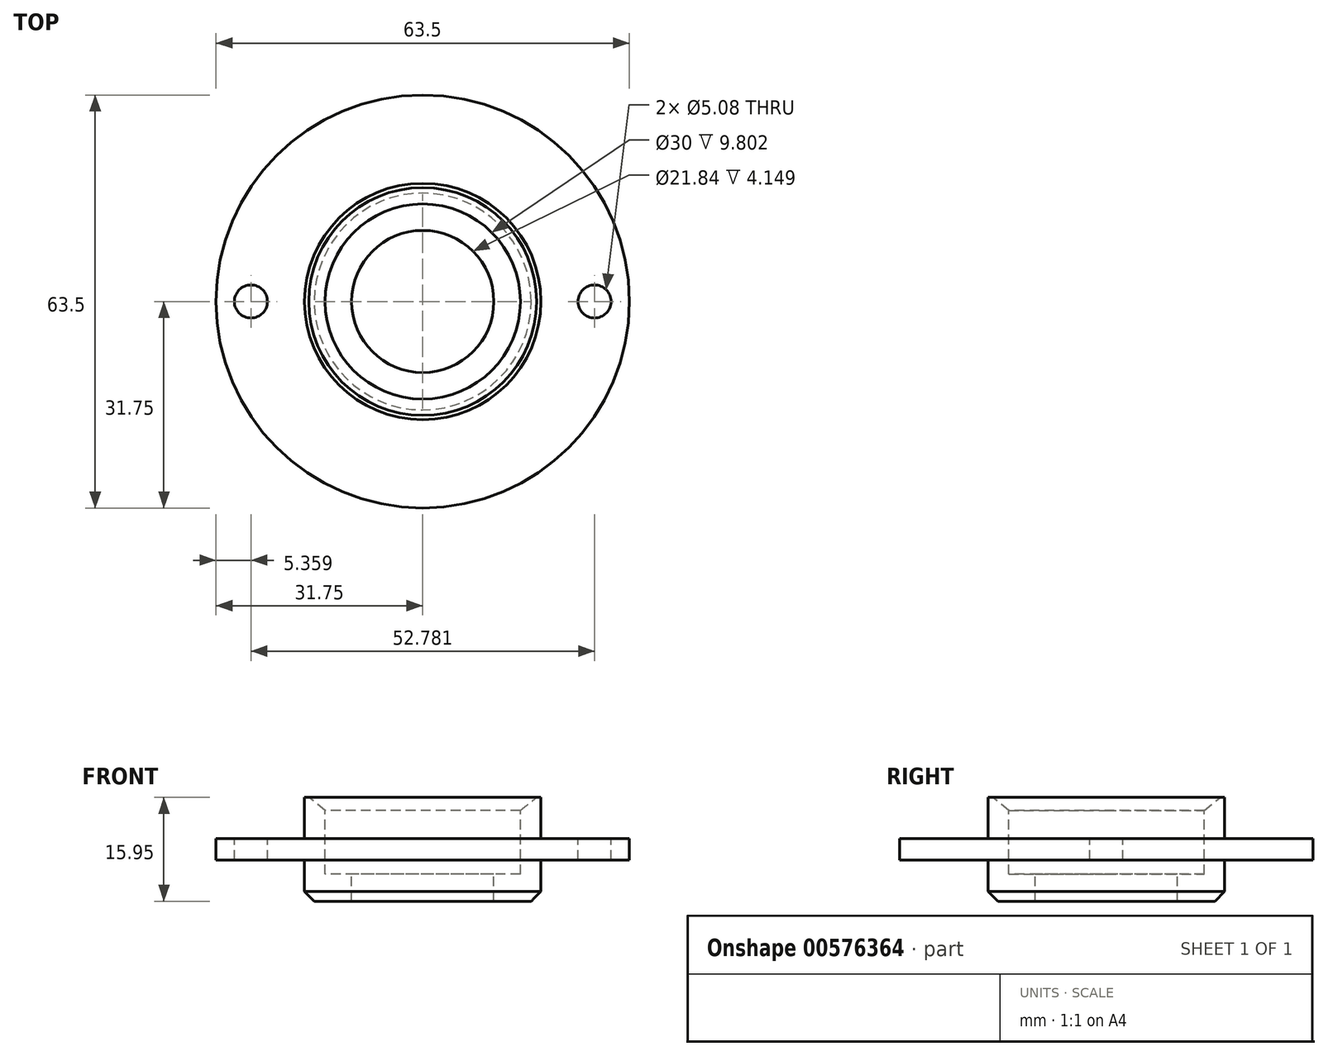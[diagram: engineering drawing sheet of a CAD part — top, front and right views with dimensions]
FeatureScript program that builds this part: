
annotation { "Feature Type Name" : "Feature", "Feature Type Description" : "" }
export const myFeature = defineFeature(function(context is Context, id is Id, definition is map)
    precondition{}
    {
        {
            var Q0;
            Q0=qCreatedBy(makeId("Front.planeOp"),FACE);
            var sketch = newSketch(context, id + "F0", { "sketchPlane" : qUnion([Q0])});
            skLineSegment(sketch, "E0", {"start": v(0, 6.57) * mm, "end": v(0, -16.88) * mm, "construction": true});
            skLineSegment(sketch, "E1", {"start": v(31.75, -2.73) * mm, "end": v(31.75, -5.98) * mm});
            skLineSegment(sketch, "E2", {"start": v(18.16, 3.62) * mm, "end": v(18.16, -2.73) * mm});
            skLineSegment(sketch, "E3", {"start": v(18.16, -5.98) * mm, "end": v(18.16, -12.33) * mm});
            skLineSegment(sketch, "E4", {"start": v(18.16, -2.73) * mm, "end": v(31.75, -2.73) * mm});
            skLineSegment(sketch, "E5", {"start": v(18.16, -5.98) * mm, "end": v(31.75, -5.98) * mm});
            skLineSegment(sketch, "E6", {"start": v(10.92, -12.33) * mm, "end": v(10.92, -8.18) * mm});
            skLineSegment(sketch, "E7", {"start": v(15, -8.18) * mm, "end": v(10.92, -8.18) * mm});
            skLineSegment(sketch, "E8", {"start": v(15, -8.18) * mm, "end": v(15, 3.62) * mm});
            skLineSegment(sketch, "E9", {"start": v(15, 3.62) * mm, "end": v(18.16, 3.62) * mm});
            skLineSegment(sketch, "E10", {"start": v(10.92, -12.33) * mm, "end": v(18.16, -12.33) * mm});
            skSolve(sketch);
        }
        {
            var Q0;
            Q0 = qSketchRegion(id + "F0", true);
            var Q1;
            Q1=sQuery(id+"F0.wireOp",EDGE,"E0");
            revolve(context, id + "F1", {"surfaceOperationType" : NewSurfaceOperationType.NEW, "entities" : qUnion([Q0]), "axis" : qUnion([Q1]), "revolveType" : RevolveType.FULL});
        }
        {
            var Q0;
            Q0=makeQuery(id+"F1.opRevolve","SWEPT_FACE",FACE,{"disambiguationData":[OSD([sQuery(id+"F0.wireOp",EDGE,"E4")])]});
            var sketch = newSketch(context, id + "F2", { "sketchPlane" : qUnion([Q0])});
            skLineSegment(sketch, "E11", {"start": v(0, 34.52) * mm, "end": v(0, -35.4) * mm, "construction": true});
            skLineSegment(sketch, "E12", {"start": v(-35.25, 0) * mm, "end": v(35.25, 0) * mm, "construction": true});
            skCircle(sketch, "E13", {"center": v(0, 0) * mm, "radius": 26.4 * mm, "construction": true});
            skCircle(sketch, "E14", {"center": v(26.4, 0) * mm, "radius": 2.54 * mm});
            skCircle(sketch, "E15", {"center": v(-26.4, 0) * mm, "radius": 2.54 * mm});
            skSolve(sketch);
        }
        {
            var Q0;
            Q0 = qSketchRegion(id + "F2", true);
            extrude(context, id + "F3", {"entities" : qUnion([Q0]), "operationType" : NewBodyOperationType.REMOVE, "endBound" : BoundingType.THROUGH_ALL, "oppositeDirection" : true, "depth" : 25 * mm, "offsetDistance" : 25 * mm});
        }
        {
            var Q0;
            Q0=makeQuery(id+"F1.opRevolve","SWEPT_EDGE",EDGE,{"disambiguationData":[OSD([sQuery(id+"F0.wireOp",EDGE,"E3"),sQuery(id+"F0.wireOp",EDGE,"E10")])]});
            chamfer(context, id + "F4", {"entities" : qUnion([Q0]), "width" : 1.5 * mm, "tangentPropagation" : true});
        }
        {
            var Q0;
            Q0=makeQuery(id+"F1.opRevolve","SWEPT_EDGE",EDGE,{"disambiguationData":[OSD([sQuery(id+"F0.wireOp",EDGE,"E8"),sQuery(id+"F0.wireOp",EDGE,"E9")])]});
            chamfer(context, id + "F5", {"entities" : qUnion([Q0]), "chamferType" : ChamferType.TWO_OFFSETS, "width1" : 2 * mm, "oppositeDirection" : false, "width2" : 2.5 * mm, "tangentPropagation" : true});
        }
    });
